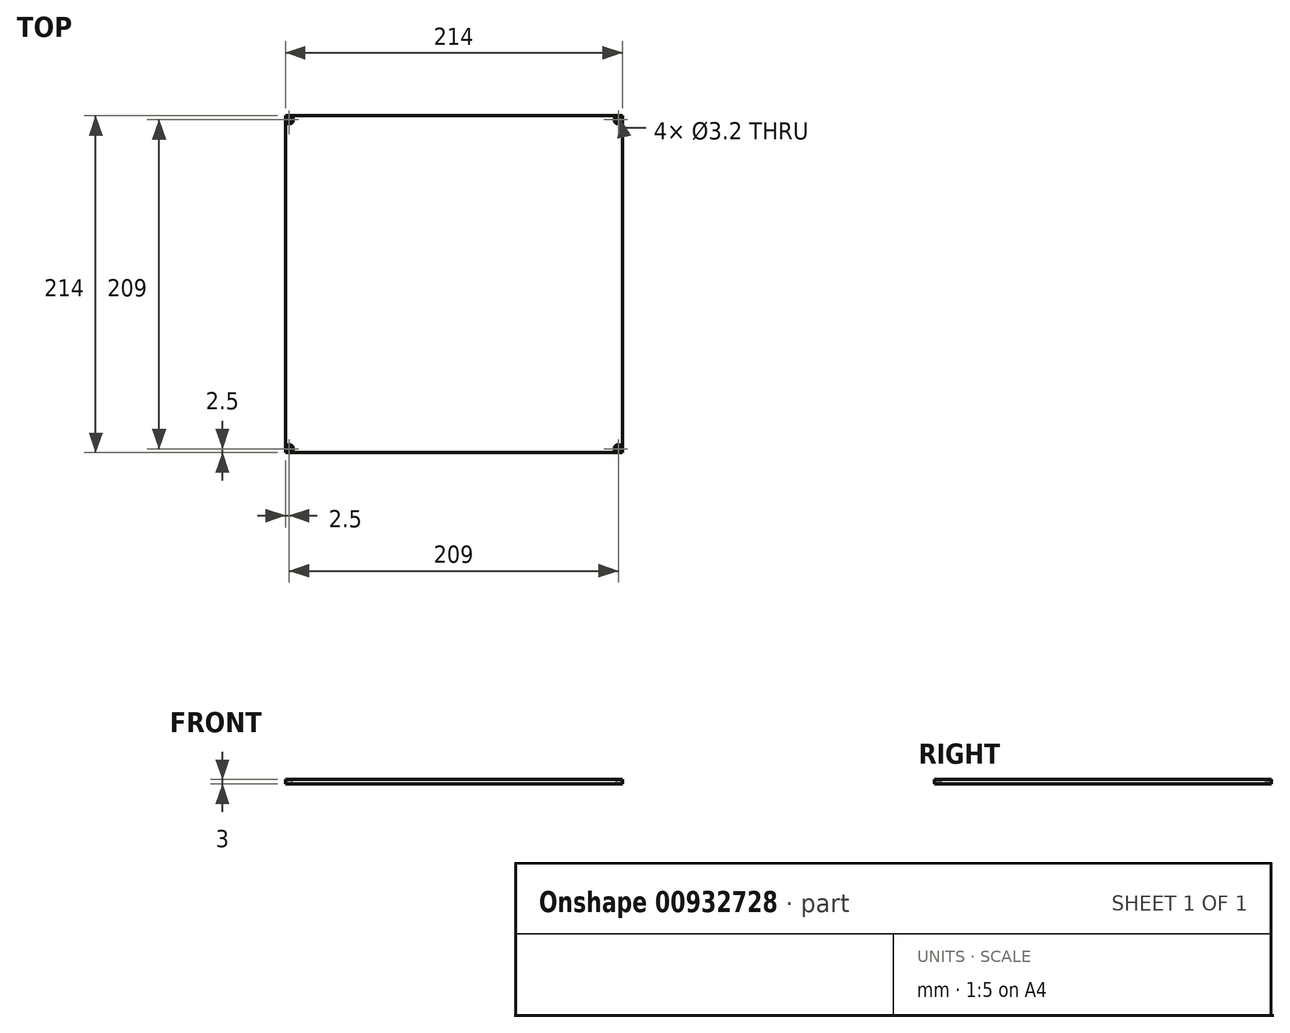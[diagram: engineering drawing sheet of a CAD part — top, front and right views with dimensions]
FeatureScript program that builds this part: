
annotation { "Feature Type Name" : "Feature", "Feature Type Description" : "" }
export const myFeature = defineFeature(function(context is Context, id is Id, definition is map)
    precondition{}
    {
        {
            var Q0;
            Q0=qCreatedBy(makeId("Top.planeOp"),FACE);
            var sketch = newSketch(context, id + "F0", { "sketchPlane" : qUnion([Q0])});
            skLineSegment(sketch, "E0", {"start": v(-107, 0) * mm, "end": v(-107, 107) * mm});
            skLineSegment(sketch, "E1", {"start": v(-107, 107) * mm, "end": v(0, 107) * mm});
            skLineSegment(sketch, "E2.MirrorCS", {"start": v(107, 0) * mm, "end": v(107, 107) * mm});
            skLineSegment(sketch, "E3.MirrorCS", {"start": v(-107, -107) * mm, "end": v(0, -107) * mm});
            skLineSegment(sketch, "E4.MirrorCS", {"start": v(-107, 0) * mm, "end": v(-107, -107) * mm});
            skLineSegment(sketch, "E5.MirrorCS", {"start": v(107, 0) * mm, "end": v(107, -107) * mm});
            skLineSegment(sketch, "E6.MirrorCS", {"start": v(107, 107) * mm, "end": v(0, 107) * mm});
            skLineSegment(sketch, "E7.MirrorCS", {"start": v(107, -107) * mm, "end": v(0, -107) * mm});
            skCircle(sketch, "E8", {"center": v(-104.5, 104.5) * mm, "radius": 1.6 * mm});
            skCircle(sketch, "E9.MirrorC", {"center": v(104.5, 104.5) * mm, "radius": 1.6 * mm});
            skCircle(sketch, "E10.MirrorC", {"center": v(-104.5, -104.5) * mm, "radius": 1.6 * mm});
            skCircle(sketch, "E11.MirrorC", {"center": v(104.5, -104.5) * mm, "radius": 1.6 * mm});
            skSolve(sketch);
        }
        {
            var Q0;
            Q0=makeQuery(id+"F0.imprint","IMPRINT",FACE,{"disambiguationData":[TD([[makeQuery(id+"F0.imprint","IMPRINT",EDGE,{"derivedFrom":sQuery(id+"F0.wireOp",EDGE,"E0")}),-1.0]])]});
            extrude(context, id + "F1", {"entities" : qUnion([Q0]), "depth" : 3 * mm, "offsetDistance" : 25 * mm});
        }
        {
            var Q0;
            Q0=makeQuery(id+"F1.opExtrude","CAP_EDGE",EDGE,{"disambiguationData":[OSD([sQuery(id+"F0.wireOp",EDGE,"E10.MirrorC")])],"isStart":false});
            var Q1;
            Q1=makeQuery(id+"F1.opExtrude","CAP_EDGE",EDGE,{"disambiguationData":[OSD([sQuery(id+"F0.wireOp",EDGE,"E8")])],"isStart":false});
            var Q2;
            Q2=makeQuery(id+"F1.opExtrude","CAP_EDGE",EDGE,{"disambiguationData":[OSD([sQuery(id+"F0.wireOp",EDGE,"E9.MirrorC")])],"isStart":false});
            var Q3;
            Q3=makeQuery(id+"F1.opExtrude","CAP_EDGE",EDGE,{"disambiguationData":[OSD([sQuery(id+"F0.wireOp",EDGE,"E11.MirrorC")])],"isStart":false});
            chamfer(context, id + "F2", {"entities" : qUnion([Q0, Q1, Q2, Q3]), "width" : 1 * mm, "tangentPropagation" : true});
        }
    });
